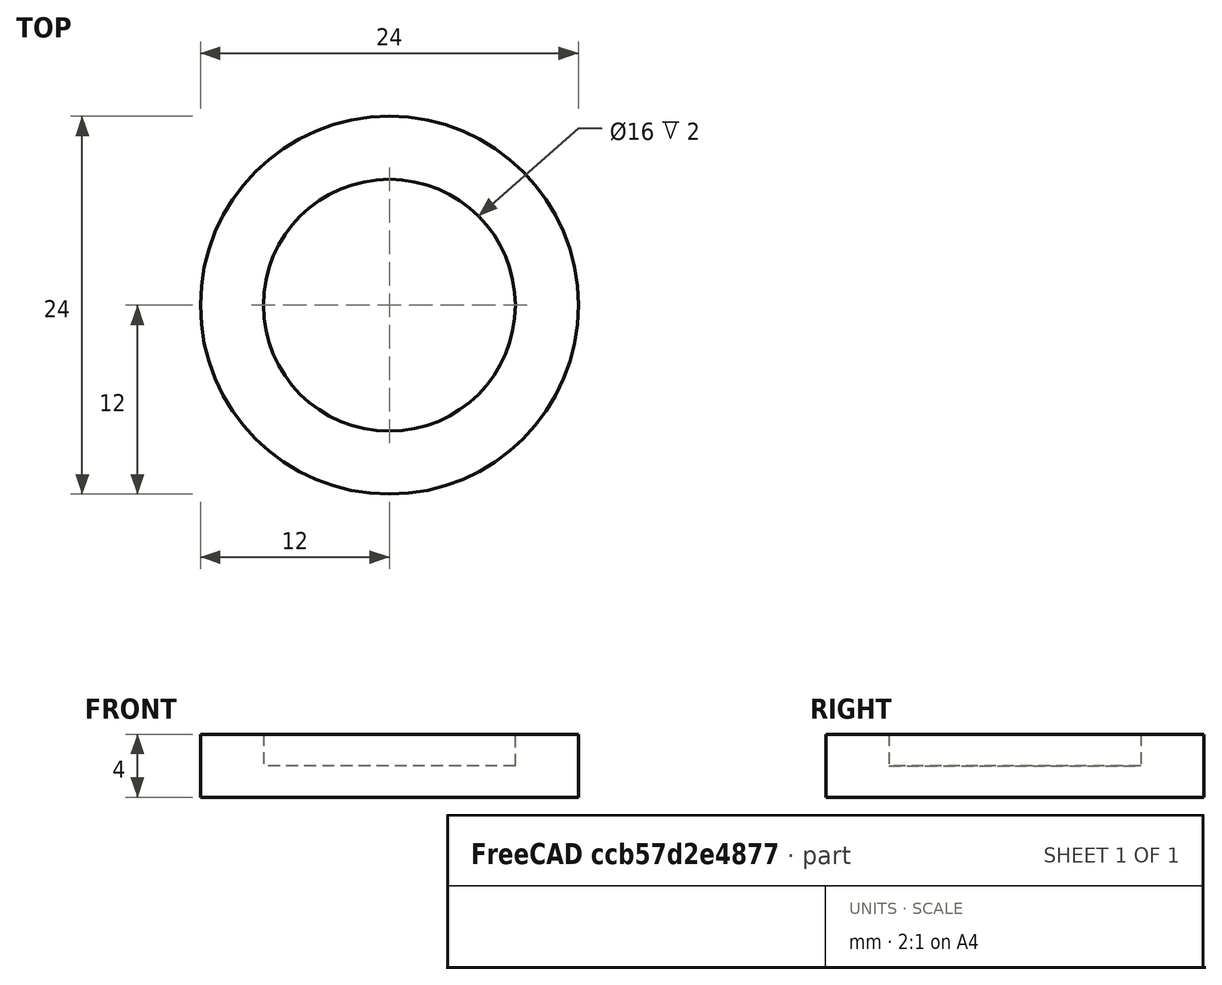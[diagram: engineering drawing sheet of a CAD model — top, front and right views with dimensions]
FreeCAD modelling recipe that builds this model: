
FCSTD DOCUMENT  (FreeCAD 0.18.4R)
Label: car-wheel
License: All rights reserved
LicenseURL: http://en.wikipedia.org/wiki/All_rights_reserved
objects: Sketcher::SketchObject×2, PartDesign::Pad×1, PartDesign::Pocket×1, PartDesign::Body×1
note: 7 computed .brp shape members not serialized (recipe doc carries the construction recipe); baked Part::Feature solids carry a one-line shape summary decoded from their .brp

FEATURE [Sketcher::SketchObject] Sketch
  MapMode = 5
  Support = -> [XY_Plane]
  sketch-geometry (1):
    g0: Circle CenterX=0 CenterY=0 CenterZ=0 NormalX=0 NormalY=0 NormalZ=1 AngleXU=0 Radius=12
  constraints (1):
    c: Radius(g0) = 12
FEATURE [PartDesign::Pad] Pad
  Length = 4
  Length2 = 100
  Midplane = true
  Profile = -> Sketch
  Type = 0
FEATURE [Sketcher::SketchObject] Sketch001
  MapMode = 5
  Support = -> [XY_Plane]
  sketch-geometry (1):
    g0: Circle CenterX=0 CenterY=0 CenterZ=0 NormalX=0 NormalY=0 NormalZ=1 AngleXU=0 Radius=8
  constraints (2):
    c: Coincident(g0,g-1)
    c: Radius(g0) = 8
FEATURE [PartDesign::Pocket] Pocket
  BaseFeature = -> Pad
  Length = 2
  Length2 = 100
  Profile = -> Sketch001
  Reversed = true
  Type = 0
FEATURE [PartDesign::Body] Body
  Group = -> [Sketch,Pad,Sketch001,Pocket]
  Origin = -> Origin
  Tip = -> Pocket
